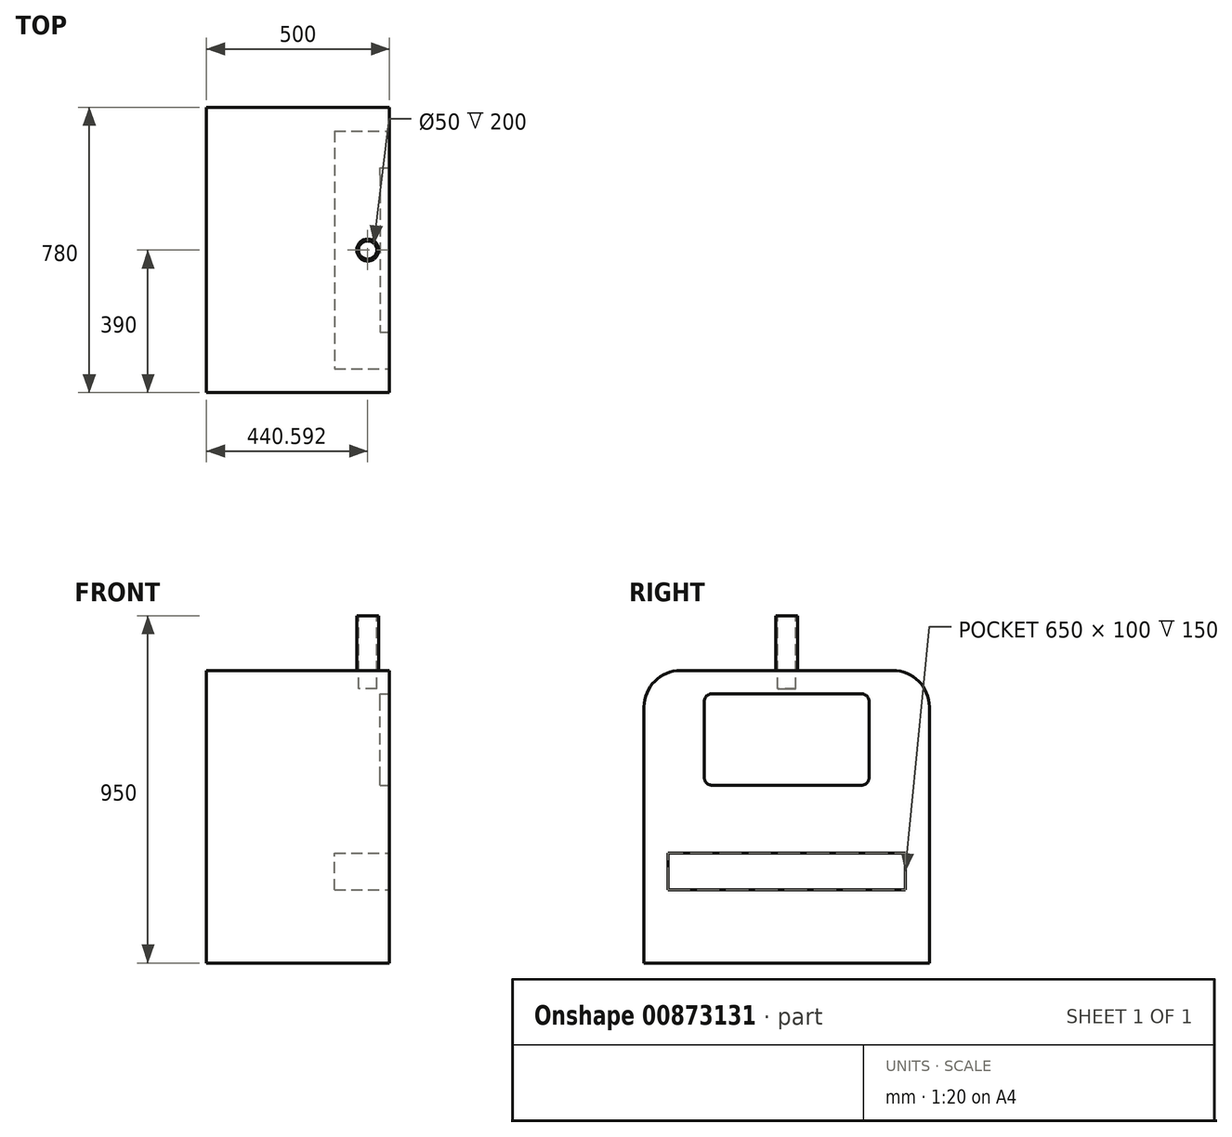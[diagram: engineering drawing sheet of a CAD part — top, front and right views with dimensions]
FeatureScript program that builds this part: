
annotation { "Feature Type Name" : "Feature", "Feature Type Description" : "" }
export const myFeature = defineFeature(function(context is Context, id is Id, definition is map)
    precondition{}
    {
        {
            var Q0;
            Q0=qCreatedBy(makeId("Right.planeOp"),FACE);
            var sketch = newSketch(context, id + "F0", { "sketchPlane" : qUnion([Q0])});
            skLineSegment(sketch, "E0.bottom", {"start": v(390, -400) * mm, "end": v(-390, -400) * mm});
            skLineSegment(sketch, "E0.top", {"start": v(390, 400) * mm, "end": v(-390, 400) * mm});
            skLineSegment(sketch, "E0.left", {"start": v(390, -400) * mm, "end": v(390, 400) * mm});
            skLineSegment(sketch, "E0.right", {"start": v(-390, -400) * mm, "end": v(-390, 400) * mm});
            skPoint(sketch, "E0.middle", {"position": v(0, 0) * mm});
            skSolve(sketch);
        }
        {
            var Q0;
            Q0 = qSketchRegion(id + "F0", true);
            extrude(context, id + "F1", {"entities" : qUnion([Q0]), "oppositeDirection" : true, "depth" : 500 * mm, "offsetDistance" : 25 * mm});
        }
        {
            var Q0;
            Q0=makeQuery(id+"F1.opExtrude","SWEPT_EDGE",EDGE,{"disambiguationData":[OSD([sQuery(id+"F0.wireOp",EDGE,"E0.top"),sQuery(id+"F0.wireOp",EDGE,"E0.right")])]});
            var Q1;
            Q1=makeQuery(id+"F1.opExtrude","SWEPT_EDGE",EDGE,{"disambiguationData":[OSD([sQuery(id+"F0.wireOp",EDGE,"E0.top"),sQuery(id+"F0.wireOp",EDGE,"E0.left")])]});
            fillet(context, id + "F2", {"entities" : qUnion([Q0, Q1]), "radius" : 100 * mm, "tangentPropagation" : true, "allowEdgeOverflow" : false});
        }
        {
            var Q0;
            Q0=makeQuery(id+"F1.opExtrude","SWEPT_FACE",FACE,{"disambiguationData":[OSD([sQuery(id+"F0.wireOp",EDGE,"E0.top")])]});
            var sketch = newSketch(context, id + "F3", { "sketchPlane" : qUnion([Q0])});
            skCircle(sketch, "E1", {"center": v(-59.4, 0) * mm, "radius": 30 * mm});
            skSolve(sketch);
        }
        {
            var Q0;
            Q0 = qSketchRegion(id + "F3", true);
            extrude(context, id + "F4", {"entities" : qUnion([Q0]), "operationType" : NewBodyOperationType.ADD, "depth" : 150 * mm, "offsetDistance" : 25 * mm});
        }
        {
            var Q0;
            Q0=makeQuery(id+"F4.opExtrude","CAP_FACE",FACE,{"disambiguationData":[OSD([sQuery(id+"F3.wireOp",EDGE,"E1")])],"isStart":false});
            var sketch = newSketch(context, id + "F5", { "sketchPlane" : qUnion([Q0])});
            skCircle(sketch, "E2", {"center": v(-59.4, 0) * mm, "radius": 25 * mm});
            skSolve(sketch);
        }
        {
            var Q0;
            Q0 = qSketchRegion(id + "F5", true);
            extrude(context, id + "F6", {"entities" : qUnion([Q0]), "operationType" : NewBodyOperationType.REMOVE, "oppositeDirection" : true, "depth" : 200 * mm, "offsetDistance" : 25 * mm});
        }
        {
            var Q0;
            Q0=makeQuery(id+"F1.opExtrude","CAP_FACE",FACE,{"disambiguationData":[OSD([sQuery(id+"F0.wireOp",EDGE,"E0.bottom"),sQuery(id+"F0.wireOp",EDGE,"E0.top"),sQuery(id+"F0.wireOp",EDGE,"E0.left"),sQuery(id+"F0.wireOp",EDGE,"E0.right")])],"isStart":true});
            var sketch = newSketch(context, id + "F7", { "sketchPlane" : qUnion([Q0])});
            skLineSegment(sketch, "E3.bottom", {"start": v(225, 86.29) * mm, "end": v(-225, 86.29) * mm});
            skLineSegment(sketch, "E3.top", {"start": v(225, 336.29) * mm, "end": v(-225, 336.29) * mm});
            skLineSegment(sketch, "E3.left", {"start": v(225, 86.29) * mm, "end": v(225, 336.29) * mm});
            skLineSegment(sketch, "E3.right", {"start": v(-225, 86.29) * mm, "end": v(-225, 336.29) * mm});
            skPoint(sketch, "E3.middle", {"position": v(0, 211.29) * mm});
            skSolve(sketch);
        }
        {
            var Q0;
            Q0=makeQuery(id+"F7.imprint","IMPRINT",FACE,{"disambiguationData":[TD([[makeQuery(id+"F7.imprint","IMPRINT",EDGE,{"derivedFrom":sQuery(id+"F7.wireOp",EDGE,"E3.bottom")}),-1.0]])]});
            extrude(context, id + "F8", {"entities" : qUnion([Q0]), "operationType" : NewBodyOperationType.REMOVE, "oppositeDirection" : true, "depth" : 25 * mm, "offsetDistance" : 25 * mm});
        }
        {
            var Q0;
            Q0=makeQuery(id+"F8.boolean.opBoolean","COPY",EDGE,{"derivedFrom":makeQuery(id+"F8.opExtrude","SWEPT_EDGE",EDGE,{"disambiguationData":[OSD([sQuery(id+"F7.wireOp",EDGE,"E3.top"),sQuery(id+"F7.wireOp",EDGE,"E3.right")])]})});
            var Q1;
            Q1=makeQuery(id+"F8.boolean.opBoolean","COPY",EDGE,{"derivedFrom":makeQuery(id+"F8.opExtrude","SWEPT_EDGE",EDGE,{"disambiguationData":[OSD([sQuery(id+"F7.wireOp",EDGE,"E3.top"),sQuery(id+"F7.wireOp",EDGE,"E3.left")])]})});
            var Q2;
            Q2=makeQuery(id+"F8.boolean.opBoolean","COPY",EDGE,{"derivedFrom":makeQuery(id+"F8.opExtrude","SWEPT_EDGE",EDGE,{"disambiguationData":[OSD([sQuery(id+"F7.wireOp",EDGE,"E3.bottom"),sQuery(id+"F7.wireOp",EDGE,"E3.right")])]})});
            var Q3;
            Q3=makeQuery(id+"F8.boolean.opBoolean","COPY",EDGE,{"derivedFrom":makeQuery(id+"F8.opExtrude","SWEPT_EDGE",EDGE,{"disambiguationData":[OSD([sQuery(id+"F7.wireOp",EDGE,"E3.bottom"),sQuery(id+"F7.wireOp",EDGE,"E3.left")])]})});
            fillet(context, id + "F9", {"entities" : qUnion([Q0, Q1, Q2, Q3]), "radius" : 20 * mm, "tangentPropagation" : true, "allowEdgeOverflow" : false});
        }
        {
            var Q0;
            Q0=makeQuery(id+"F1.opExtrude","CAP_FACE",FACE,{"disambiguationData":[OSD([sQuery(id+"F0.wireOp",EDGE,"E0.bottom"),sQuery(id+"F0.wireOp",EDGE,"E0.top"),sQuery(id+"F0.wireOp",EDGE,"E0.left"),sQuery(id+"F0.wireOp",EDGE,"E0.right")])],"isStart":true});
            var sketch = newSketch(context, id + "F10", { "sketchPlane" : qUnion([Q0])});
            skLineSegment(sketch, "E4.bottom", {"start": v(325, -200) * mm, "end": v(-325, -200) * mm});
            skLineSegment(sketch, "E4.top", {"start": v(325, -100) * mm, "end": v(-325, -100) * mm});
            skLineSegment(sketch, "E4.left", {"start": v(325, -200) * mm, "end": v(325, -100) * mm});
            skLineSegment(sketch, "E4.right", {"start": v(-325, -200) * mm, "end": v(-325, -100) * mm});
            skPoint(sketch, "E4.middle", {"position": v(0, -150) * mm});
            skLineSegment(sketch, "E5", {"start": v(0, -150) * mm, "end": v(0, -400) * mm});
            skSolve(sketch);
        }
        {
            var Q0;
            Q0=makeQuery(id+"F10.imprint","IMPRINT",FACE,{"disambiguationData":[TD([[makeQuery(id+"F10.imprint","IMPRINT",EDGE,{"derivedFrom":sQuery(id+"F10.wireOp",EDGE,"E4.top")}),1.0]])]});
            extrude(context, id + "F11", {"entities" : qUnion([Q0]), "operationType" : NewBodyOperationType.REMOVE, "oppositeDirection" : true, "depth" : 150 * mm, "offsetDistance" : 25 * mm});
        }
    });
